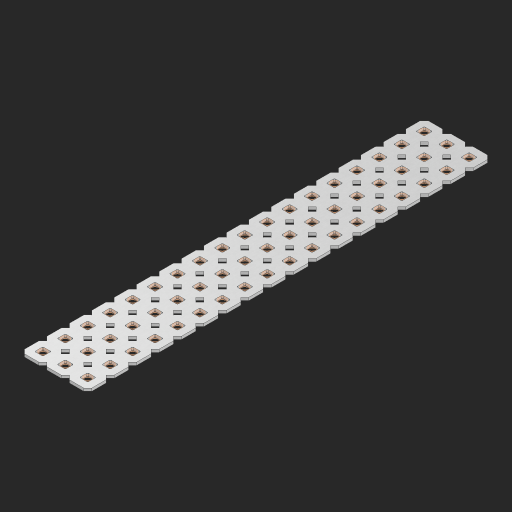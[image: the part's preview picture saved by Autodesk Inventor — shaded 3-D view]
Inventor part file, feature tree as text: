
AUTODESK INVENTOR PART (.ipt)
format: ipt  version: 2023 (Build 270158000, 158)  size: 902,656 bytes
history: native  units: in
note: dims shown in document units (in); Inventor stores cm internally (conversion verified against a paired STEP export)
features: other x55, extrude x53, sketch x2, pattern_linear x1
ambient origin geometry x8: Origin, YZ Plane, XZ Plane, XY Plane, X Axis, Y Axis, Z Axis, Center Point
bodies: Solid1 (feature_tree), Body (feature_tree)
feature tree (111):
  pattern_linear  "Rectangular Pattern1"  Spacing1=0.09in  [1 undecoded]
  sketch  "Sketch1"  dims[d1=0.5in]
  sketch  "Sketch2"  dims[d2=0.182in d3=0.09in d4=0.09in d5=0.09in d6=0.09in d7=0.09in d8=0.09in d9=0.09in d10=0.09in d11=0.02in d13=0.0in d14=0.172in d15=0.0625in d16=0.0in d19=0.5in d22=0.5in]
  other  "Srf1"
  other  "Srf126"
  other  "Srf127"
  other  "Srf128"
  other  "Srf129"
  other  "Srf130"
  other  "Srf131"
  other  "Srf250"
  other  "Srf251"
  other  "Srf252"
  other  "Srf253"
  other  "Srf254"
  other  "Srf255"
  other  "Srf256"
  other  "Srf257"
  other  "Srf258"
  other  "Srf259"
  other  "Srf260"
  other  "Srf268"
  other  "Srf269"
  other  "Srf270"
  other  "Srf271"
  other  "Srf272"
  other  "Srf273"
  other  "Srf274"
  other  "Srf275"
  other  "Srf276"
  other  "Srf277"
  other  "Srf278"
  other  "Srf279"
  other  "Srf280"
  other  "Srf281"
  other  "Srf282"
  other  "Srf283"
  other  "Srf284"
  other  "Srf285"
  other  "Srf293"
  other  "Srf294"
  other  "Srf295"
  other  "Srf296"
  other  "Srf297"
  other  "Srf298"
  other  "Srf299"
  other  "Srf300"
  other  "Srf301"
  other  "Srf302"
  other  "Srf303"
  other  "Srf304"
  other  "Srf305"
  other  "Srf306"
  other  "Srf307"
  other  "Srf308"
  other  "Srf309"
  other  "Srf310"
  other  "Circle"
  extrude  "ExtrusionSrf126"  Depth=0.09in
  extrude  "ExtrusionSrf127"  Depth=0.09in
  extrude  "ExtrusionSrf128"  Depth=0.09in
  extrude  "ExtrusionSrf129"  Depth=0.09in
  extrude  "ExtrusionSrf130"  Depth=0.09in
  extrude  "ExtrusionSrf131"  Depth=0.09in
  extrude  "ExtrusionSrf250"  Depth=0.09in
  extrude  "ExtrusionSrf251"  Depth=0.02in
  extrude  "ExtrusionSrf252"  TaperAngle=0.0deg  [1 undecoded]
  extrude  "ExtrusionSrf253"  Depth=0.5in
  extrude  "ExtrusionSrf254"  Depth=0.0625in TaperAngle=0.0deg
  extrude  "ExtrusionSrf255"  Depth=0.5in
  extrude  "ExtrusionSrf256"  Depth=0.5in
  extrude  "ExtrusionSrf257"  [1 undecoded]
  extrude  "ExtrusionSrf258"  [1 undecoded]
  extrude  "ExtrusionSrf259"  [1 undecoded]
  extrude  "ExtrusionSrf260"  [1 undecoded]
  extrude  "ExtrusionSrf268"  [1 undecoded]
  extrude  "ExtrusionSrf269"  [1 undecoded]
  extrude  "ExtrusionSrf270"  [1 undecoded]
  extrude  "ExtrusionSrf271"  [1 undecoded]
  extrude  "ExtrusionSrf272"  [1 undecoded]
  extrude  "ExtrusionSrf273"  [1 undecoded]
  extrude  "ExtrusionSrf274"  [1 undecoded]
  extrude  "ExtrusionSrf275"  [1 undecoded]
  extrude  "ExtrusionSrf276"  [1 undecoded]
  extrude  "ExtrusionSrf277"  [1 undecoded]
  extrude  "ExtrusionSrf278"  [1 undecoded]
  extrude  "ExtrusionSrf279"  [1 undecoded]
  extrude  "ExtrusionSrf280"  [1 undecoded]
  extrude  "ExtrusionSrf281"  [1 undecoded]
  extrude  "ExtrusionSrf282"  [1 undecoded]
  extrude  "ExtrusionSrf283"  [1 undecoded]
  extrude  "ExtrusionSrf284"  [1 undecoded]
  extrude  "ExtrusionSrf285"  [1 undecoded]
  extrude  "ExtrusionSrf293"  [1 undecoded]
  extrude  "ExtrusionSrf294"  [1 undecoded]
  extrude  "ExtrusionSrf295"  [1 undecoded]
  extrude  "ExtrusionSrf296"  [1 undecoded]
  extrude  "ExtrusionSrf297"  [1 undecoded]
  extrude  "ExtrusionSrf298"  [1 undecoded]
  extrude  "ExtrusionSrf299"  [1 undecoded]
  extrude  "ExtrusionSrf300"  [1 undecoded]
  extrude  "ExtrusionSrf301"  [1 undecoded]
  extrude  "ExtrusionSrf302"  [1 undecoded]
  extrude  "ExtrusionSrf303"  [1 undecoded]
  extrude  "ExtrusionSrf304"  [1 undecoded]
  extrude  "ExtrusionSrf305"  [1 undecoded]
  extrude  "ExtrusionSrf306"  [1 undecoded]
  extrude  "ExtrusionSrf307"  [1 undecoded]
  extrude  "ExtrusionSrf308"  [1 undecoded]
  extrude  "ExtrusionSrf309"  [1 undecoded]
  extrude  "ExtrusionSrf310"  [1 undecoded]
note: 42 required parameter values undecoded (feature->parameter linkage not recoverable at this tier; creation-order binding heuristic only, values carry confidence <= 0.55)
